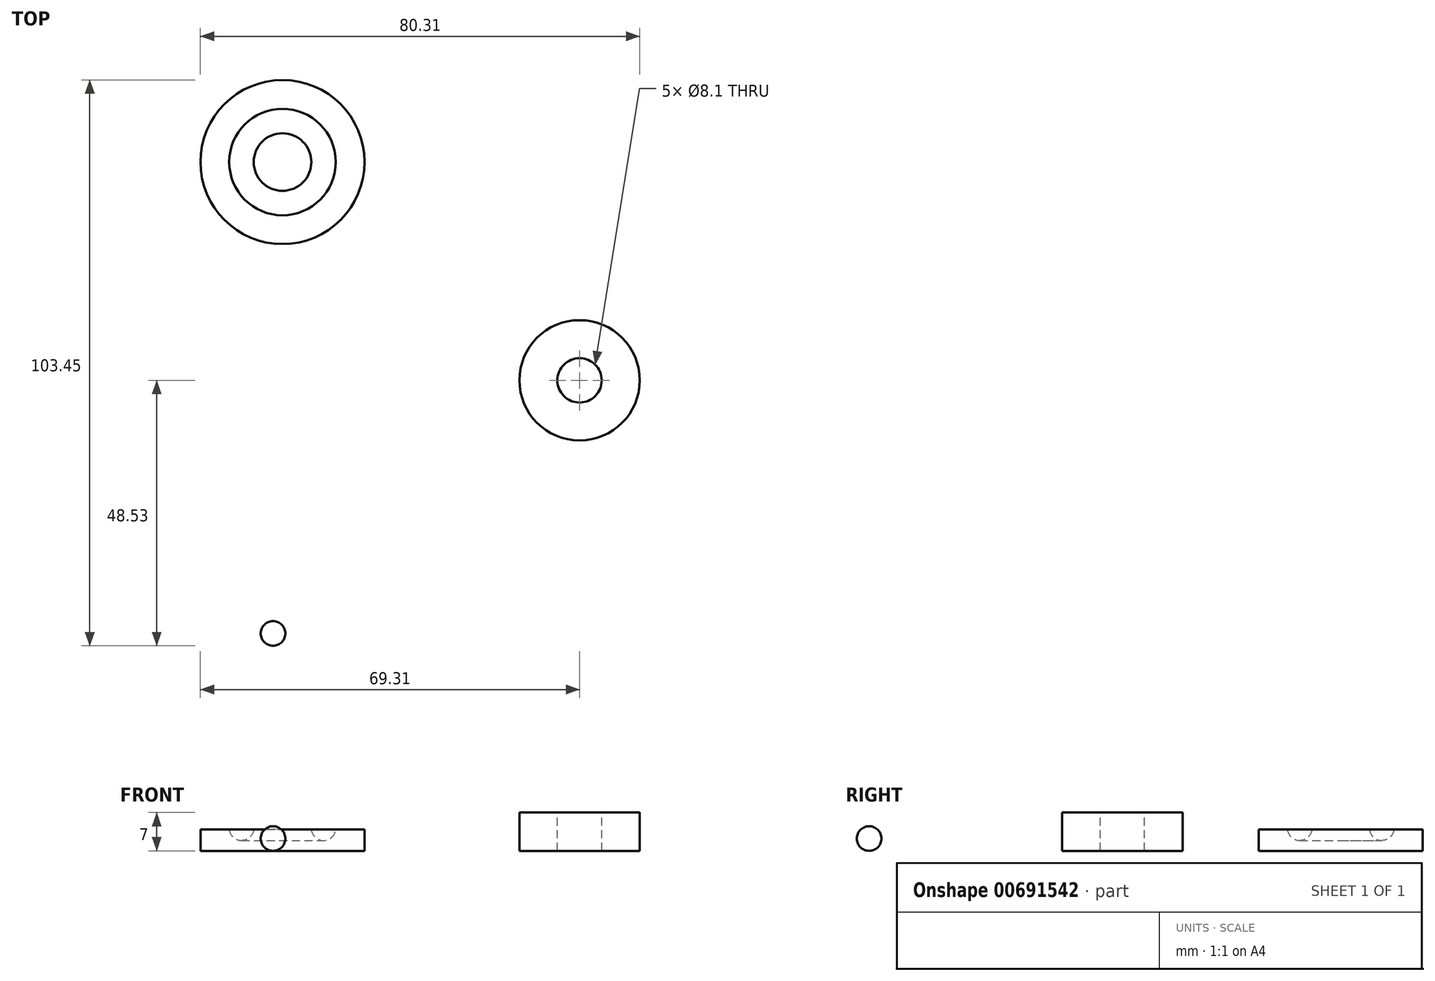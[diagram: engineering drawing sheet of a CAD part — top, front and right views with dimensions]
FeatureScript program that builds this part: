
annotation { "Feature Type Name" : "Feature", "Feature Type Description" : "" }
export const myFeature = defineFeature(function(context is Context, id is Id, definition is map)
    precondition{}
    {
        {
            var Q0;
            Q0=qCreatedBy(makeId("Top.planeOp"),FACE);
            var sketch = newSketch(context, id + "F0", { "sketchPlane" : qUnion([Q0])});
            skCircle(sketch, "E0", {"center": v(0, 0) * mm, "radius": 11 * mm});
            skCircle(sketch, "E1", {"center": v(0, 0) * mm, "radius": 2.5 * mm});
            skSolve(sketch);
        }
        {
            var Q0;
            Q0=qSketchRegion(id+"F0",true);
            extrude(context, id + "F1", {"entities" : qUnion([Q0]), "depth" : 7 * mm, "offsetDistance" : 25 * mm});
        }
        {
            var Q0;
            Q0=qCreatedBy(makeId("Top.planeOp"),FACE);
            var sketch = newSketch(context, id + "F2", { "sketchPlane" : qUnion([Q0])});
            skCircle(sketch, "E2", {"center": v(-56.03, -46.28) * mm, "radius": 2.25 * mm});
            skSolve(sketch);
        }
        {
            var Q0;
            Q0=qSketchRegion(id+"F2",true);
            extrude(context, id + "F3", {"entities" : qUnion([Q0]), "depth" : 4.5 * mm, "offsetDistance" : 25 * mm});
        }
        {
            var Q0;
            Q0=makeQuery(id+"F3.opExtrude","CAP_EDGE",EDGE,{"disambiguationData":[OSD([sQuery(id+"F2.wireOp",EDGE,"E2")])],"isStart":false});
            var Q1;
            Q1=makeQuery(id+"F3.opExtrude","CAP_EDGE",EDGE,{"disambiguationData":[OSD([sQuery(id+"F2.wireOp",EDGE,"E2")])],"isStart":true});
            fillet(context, id + "F4", {"entities" : qUnion([Q0, Q1]), "radius" : (4.5 / 2) * mm, "tangentPropagation" : true, "allowEdgeOverflow" : false});
        }
        {
            var Q0;
            Q0=qCreatedBy(makeId("Top.planeOp"),FACE);
            var sketch = newSketch(context, id + "F5", { "sketchPlane" : qUnion([Q0])});
            skCircle(sketch, "E3", {"center": v(-54.3, 39.92) * mm, "radius": 15 * mm});
            skSolve(sketch);
        }
        {
            var Q0;
            Q0=makeQuery(id+"F5.imprint","IMPRINT",FACE,{"disambiguationData":[TD([[makeQuery(id+"F5.imprint","IMPRINT",EDGE,{"derivedFrom":sQuery(id+"F5.wireOp",EDGE,"E3")}),1.0]])]});
            extrude(context, id + "F6", {"entities" : qUnion([Q0]), "depth" : 3.9 * mm, "offsetDistance" : 25 * mm});
        }
        {
            var Q0;
            Q0=makeQuery(id+"F6.opExtrude","CAP_FACE",FACE,{"disambiguationData":[OSD([sQuery(id+"F5.wireOp",EDGE,"E3")])],"isStart":false});
            var sketch = newSketch(context, id + "F7", { "sketchPlane" : qUnion([Q0])});
            skCircle(sketch, "E4", {"center": v(-54.3, 39.92) * mm, "radius": 5.25 * mm});
            skCircle(sketch, "E5", {"center": v(-54.3, 39.92) * mm, "radius": 9.75 * mm});
            skLineSegment(sketch, "E6", {"start": v(-54.3, 39.92) * mm, "end": v(-49.06, 39.92) * mm, "construction": true});
            skLineSegment(sketch, "E7", {"start": v(-44.56, 39.92) * mm, "end": v(-39.3, 39.92) * mm, "construction": true});
            skSolve(sketch);
        }
        {
            var Q0;
            Q0=sQuery(id+"F7.wireOp",EDGE,"E7");
            cPlane(context, id + "F8", {"entities" : qUnion([Q0]), "cplaneType" : CPlaneType.LINE_ANGLE, "offset" : 0 * mm, "angle" : 0 * degree, "width" : 150 * mm, "height" : 150 * mm});
        }
        {
            var Q0;
            Q0=qCreatedBy(id+"F8.planeOp",FACE);
            var sketch = newSketch(context, id + "F9", { "sketchPlane" : qUnion([Q0])});
            skArc(sketch, "E8", {"start": v(44.56, 4.15) * mm, "mid": v(46.8, 1.9) * mm, "end": v(49.06, 4.15) * mm});
            skLineSegment(sketch, "E9", {"start": v(49.06, 4.15) * mm, "end": v(49.06, 3.9) * mm, "construction": true});
            skLineSegment(sketch, "E10", {"start": v(44.56, 4.15) * mm, "end": v(44.56, 3.9) * mm, "construction": true});
            skLineSegment(sketch, "E11", {"start": v(49.06, 4.15) * mm, "end": v(44.56, 4.15) * mm});
            skSolve(sketch);
        }
        {
            var Q0;
            Q0=qSketchRegion(id+"F9",true);
            var Q1;
            Q1=sQuery(id+"F7.wireOp",EDGE,"E4");
            revolve(context, id + "F10", {"operationType" : NewBodyOperationType.REMOVE, "entities" : qUnion([Q0]), "axis" : qUnion([Q1]), "revolveType" : RevolveType.FULL, "oppositeDirection" : true});
        }
        {
            var Q0;
            Q0=makeQuery(id+"F1.opExtrude","CAP_FACE",FACE,{"disambiguationData":[OSD([sQuery(id+"F0.wireOp",EDGE,"E0"),sQuery(id+"F0.wireOp",EDGE,"E1")])],"isStart":false});
            var sketch = newSketch(context, id + "F11", { "sketchPlane" : qUnion([Q0])});
            skCircle(sketch, "E12", {"center": v(0, 0) * mm, "radius": 4.05 * mm});
            skSolve(sketch);
        }
        {
            var Q0;
            Q0 = qSketchRegion(id + "F11", true);
            extrude(context, id + "F12", {"entities" : qUnion([Q0]), "operationType" : NewBodyOperationType.REMOVE, "oppositeDirection" : true, "depth" : 25 * mm, "offsetDistance" : 25 * mm});
        }
    });
